# Revit family: PIRA ROUND L
name_source: partatom
category: Lighting Fixtures
units: mm (PartAtom-declared; Revit-internal decimal feet)

## family parameters
Cut with Voids When Loaded = No
Host = Face
Light Source = No
Part Type = Normal
Room Calculation Point = No
Round Connector Dimension = Use Diameter
Shared = No

## types (1)
- PIRA ROUND L
    Apparent Load = 34 VA
    Cable Colour = Flexxica Line - Cable Black
    Default Elevation = 1219 mm
    Diffuser = Circly - Diffuser
    H = 700 mm  [stored 2.29659 ft]
    Hs = 754 mm  [stored 2.47375 ft]
    Lamp = LED
    Luminaire Colour = Flexxica Line - Black Alu
    Manufacturer = Flexxica
    Model = Pira Round L
    PET Colour = <By Category>
    Wattage Comments = 34W
    Wire Suspension = Aluminum

note: [stored X ft] marks values corroborated as IEEE doubles in the binary element streams (Revit-internal decimal feet)

## geometry (parser evidence)
native form markers: Blend x4, Sweep x16
no freeform markers — native parametric forms only
